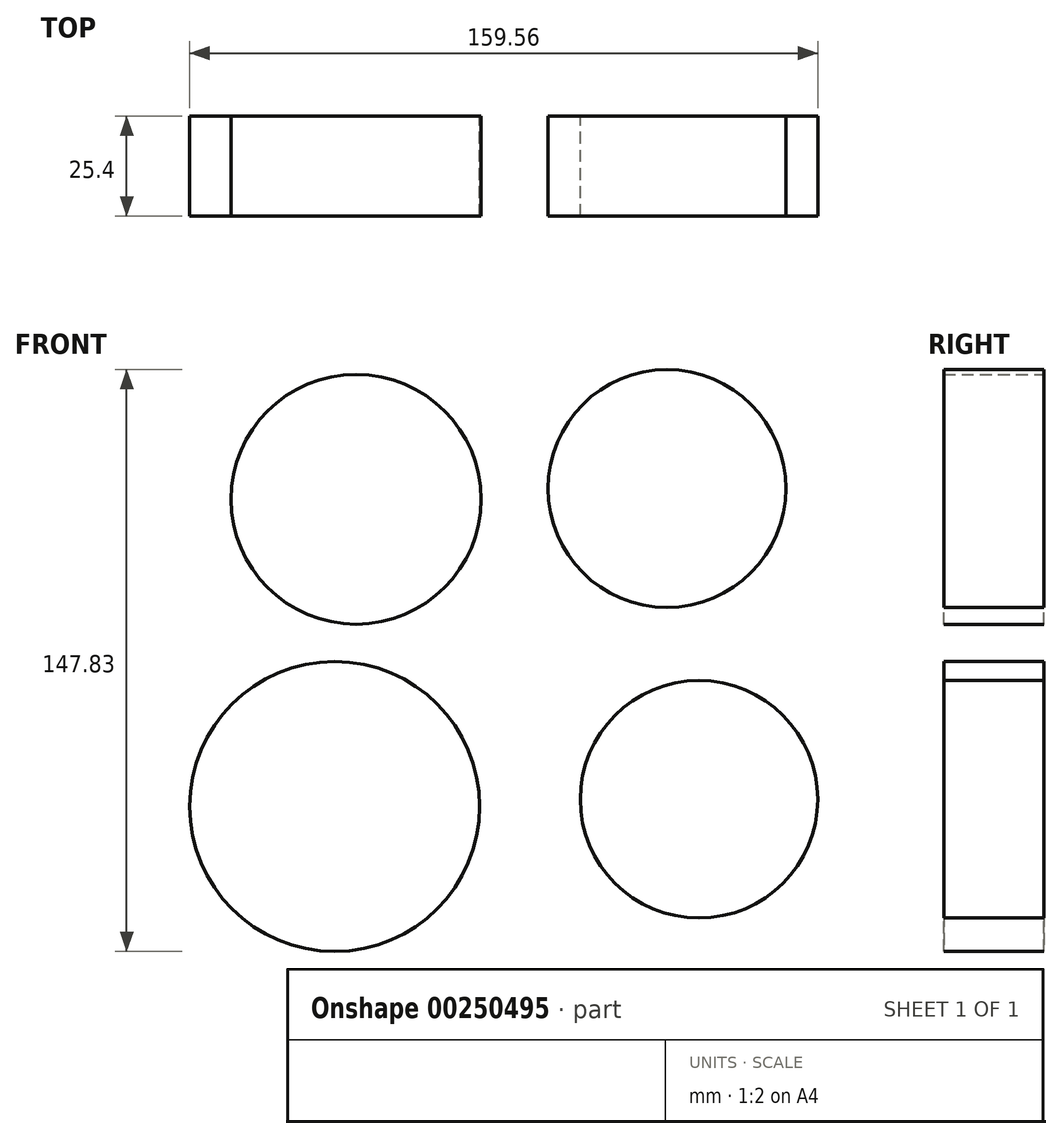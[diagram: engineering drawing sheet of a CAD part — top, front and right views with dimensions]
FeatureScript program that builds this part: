
annotation { "Feature Type Name" : "Feature", "Feature Type Description" : "" }
export const myFeature = defineFeature(function(context is Context, id is Id, definition is map)
    precondition{}
    {
        {
            var Q0;
            Q0=qCreatedBy(makeId("Front.planeOp"),FACE);
            var sketch = newSketch(context, id + "F0", { "sketchPlane" : qUnion([Q0])});
            skCircle(sketch, "E0", {"center": v(-61.06, -15.49) * mm, "radius": 31.75 * mm});
            skCircle(sketch, "E1", {"center": v(17.9, -12.76) * mm, "radius": 30.23 * mm});
            skCircle(sketch, "E2", {"center": v(-66.5, -93.54) * mm, "radius": 36.83 * mm});
            skCircle(sketch, "E3", {"center": v(26.06, -91.72) * mm, "radius": 30.16 * mm});
            skSolve(sketch);
        }
        {
            var Q0;
            Q0 = qSketchRegion(id + "F0", true);
            extrude(context, id + "F1", {"entities" : qUnion([Q0]), "depth" : 25.4 * mm});
        }
    });
